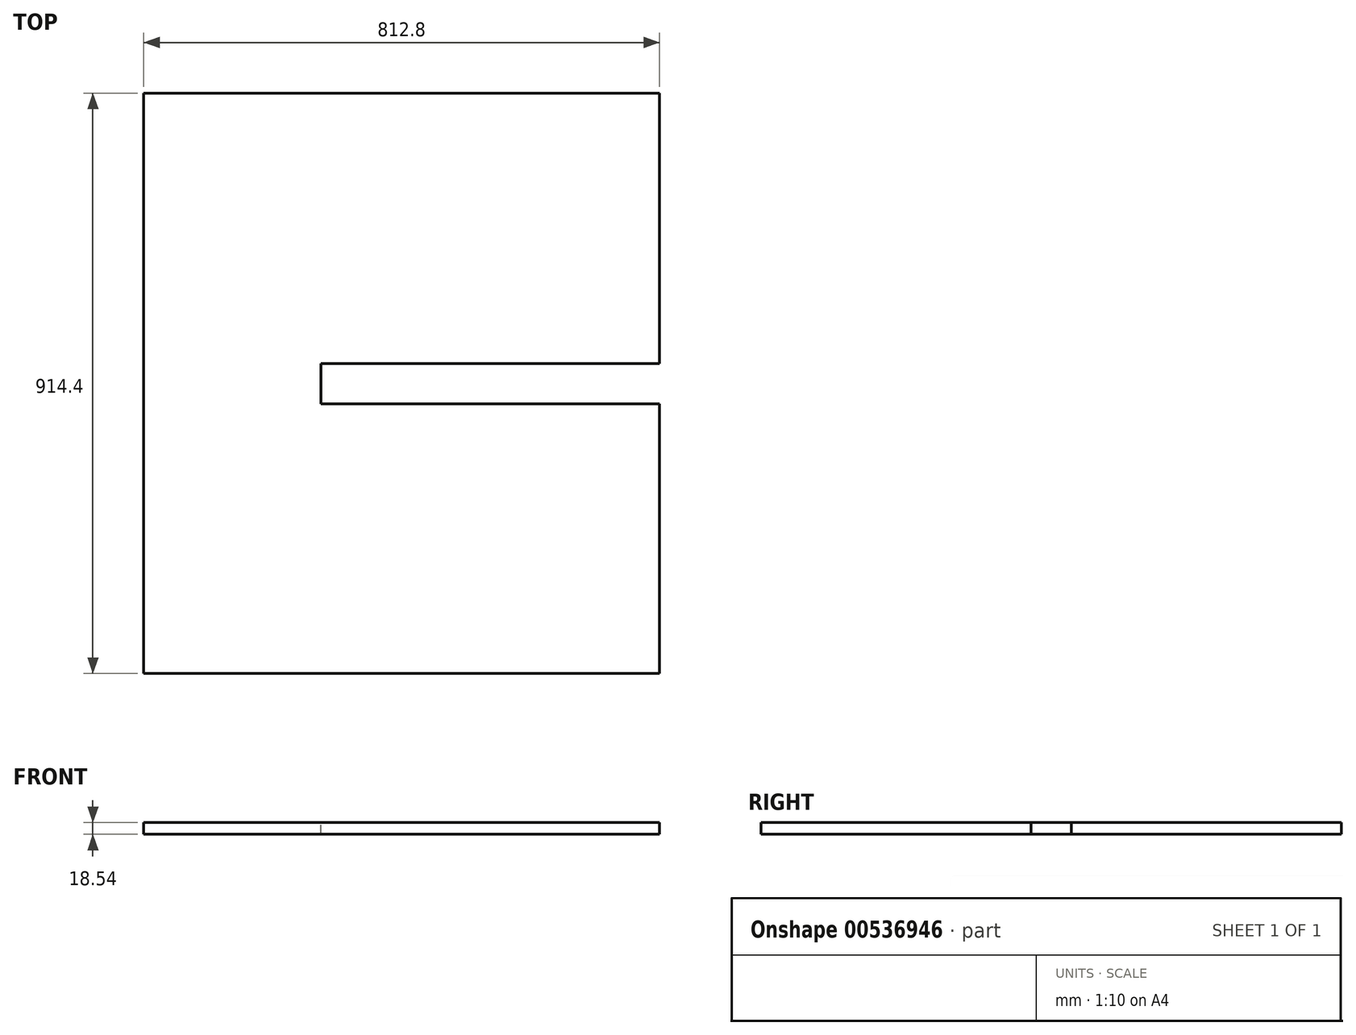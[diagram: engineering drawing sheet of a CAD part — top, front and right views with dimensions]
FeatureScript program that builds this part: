
annotation { "Feature Type Name" : "Feature", "Feature Type Description" : "" }
export const myFeature = defineFeature(function(context is Context, id is Id, definition is map)
    precondition{}
    {
        {
            var Q0;
            Q0=qCreatedBy(makeId("Top.planeOp"),FACE);
            var sketch = newSketch(context, id + "F0", { "sketchPlane" : qUnion([Q0])});
            skLineSegment(sketch, "E0.bottom", {"start": v(-2100.5, 1072.14) * mm, "end": v(337.9, 1072.14) * mm});
            skLineSegment(sketch, "E0.top", {"start": v(-2100.5, -147.06) * mm, "end": v(337.9, -147.06) * mm});
            skLineSegment(sketch, "E0.left", {"start": v(-2100.5, 1072.14) * mm, "end": v(-2100.5, -147.06) * mm});
            skLineSegment(sketch, "E0.right", {"start": v(337.9, 1072.14) * mm, "end": v(337.9, -147.06) * mm});
            skLineSegment(sketch, "E1.bottom", {"start": v(-2100.5, 1072.14) * mm, "end": v(-881.3, 1072.14) * mm});
            skLineSegment(sketch, "E1.top", {"start": v(-2100.5, 157.74) * mm, "end": v(-881.3, 157.74) * mm});
            skLineSegment(sketch, "E1.left", {"start": v(-2100.5, 1072.14) * mm, "end": v(-2100.5, 157.74) * mm});
            skLineSegment(sketch, "E1.right", {"start": v(-881.3, 1072.14) * mm, "end": v(-881.3, 157.74) * mm});
            skLineSegment(sketch, "E2", {"start": v(-2100.5, 462.54) * mm, "end": v(-2100.5, 767.34) * mm});
            skLineSegment(sketch, "E3", {"start": v(-2100.5, 462.54) * mm, "end": v(-1694.1, 157.74) * mm});
            skLineSegment(sketch, "E4", {"start": v(-1694.1, 157.74) * mm, "end": v(-1694.1, 1072.14) * mm});
            skLineSegment(sketch, "E5", {"start": v(-1694.1, 1072.14) * mm, "end": v(-2100.5, 767.34) * mm});
            skSolve(sketch);
        }
        {
            var Q0;
            {var subQ0=sQuery(id+"F0.wireOp",EDGE,"E1.right");Q0=makeQuery(id+"F0.imprint","IMPRINT",FACE,{"disambiguationData":[TD([[makeQuery(id+"F0.imprint","IMPRINT",EDGE,{"derivedFrom":subQ0}),-1.0]])]});}
            var Q1;
            Q1=makeQuery(id+"F0.imprint","IMPRINT",FACE,{"disambiguationData":[TD([[makeQuery(id+"F0.imprint","IMPRINT",EDGE,{"derivedFrom":sQuery(id+"F0.wireOp",EDGE,"E2")}),-1.0]])]});
            extrude(context, id + "F1", {"entities" : qUnion([Q0, Q1]), "depth" : 18.54 * mm, "offsetDistance" : 25.4 * mm});
        }
        {
            var Q0;
            Q0=makeQuery(id+"F1.opExtrude","CAP_FACE",FACE,{"disambiguationData":[OSD([sQuery(id+"F0.wireOp",EDGE,"E1.bottom"),sQuery(id+"F0.wireOp",EDGE,"E1.top"),sQuery(id+"F0.wireOp",EDGE,"E1.right"),sQuery(id+"F0.wireOp",EDGE,"E2"),sQuery(id+"F0.wireOp",EDGE,"E3"),sQuery(id+"F0.wireOp",EDGE,"E5")])],"isStart":false});
            var sketch = newSketch(context, id + "F2", { "sketchPlane" : qUnion([Q0])});
            skLineSegment(sketch, "E6.bottom", {"start": v(-1694.1, 1072.14) * mm, "end": v(-881.3, 1072.14) * mm});
            skLineSegment(sketch, "E6.top", {"start": v(-1694.1, 157.74) * mm, "end": v(-881.3, 157.74) * mm});
            skLineSegment(sketch, "E6.right", {"start": v(-881.3, 1072.14) * mm, "end": v(-881.3, 157.74) * mm});
            skLineSegment(sketch, "E7.bottom", {"start": v(-881.3, 582.88) * mm, "end": v(-1414.7, 582.88) * mm});
            skLineSegment(sketch, "E7.top", {"start": v(-881.3, 646.38) * mm, "end": v(-1414.7, 646.38) * mm});
            skLineSegment(sketch, "E7.left", {"start": v(-881.3, 582.88) * mm, "end": v(-881.3, 646.38) * mm});
            skLineSegment(sketch, "E7.right", {"start": v(-1414.7, 582.88) * mm, "end": v(-1414.7, 646.38) * mm});
            skPoint(sketch, "E8.orphan", {"position": v(-2100.5, 614.94) * mm});
            skPoint(sketch, "E9.end.orphan", {"position": v(-881.3, 614.94) * mm});
            skSolve(sketch);
        }
        {
            var Q0;
            Q0 = qSketchRegion(id + "F2", true);
            extrude(context, id + "F3", {"entities" : qUnion([Q0]), "operationType" : NewBodyOperationType.REMOVE, "endBound" : BoundingType.THROUGH_ALL, "oppositeDirection" : true, "depth" : 25.4 * mm, "offsetDistance" : 25.4 * mm});
        }
    });
